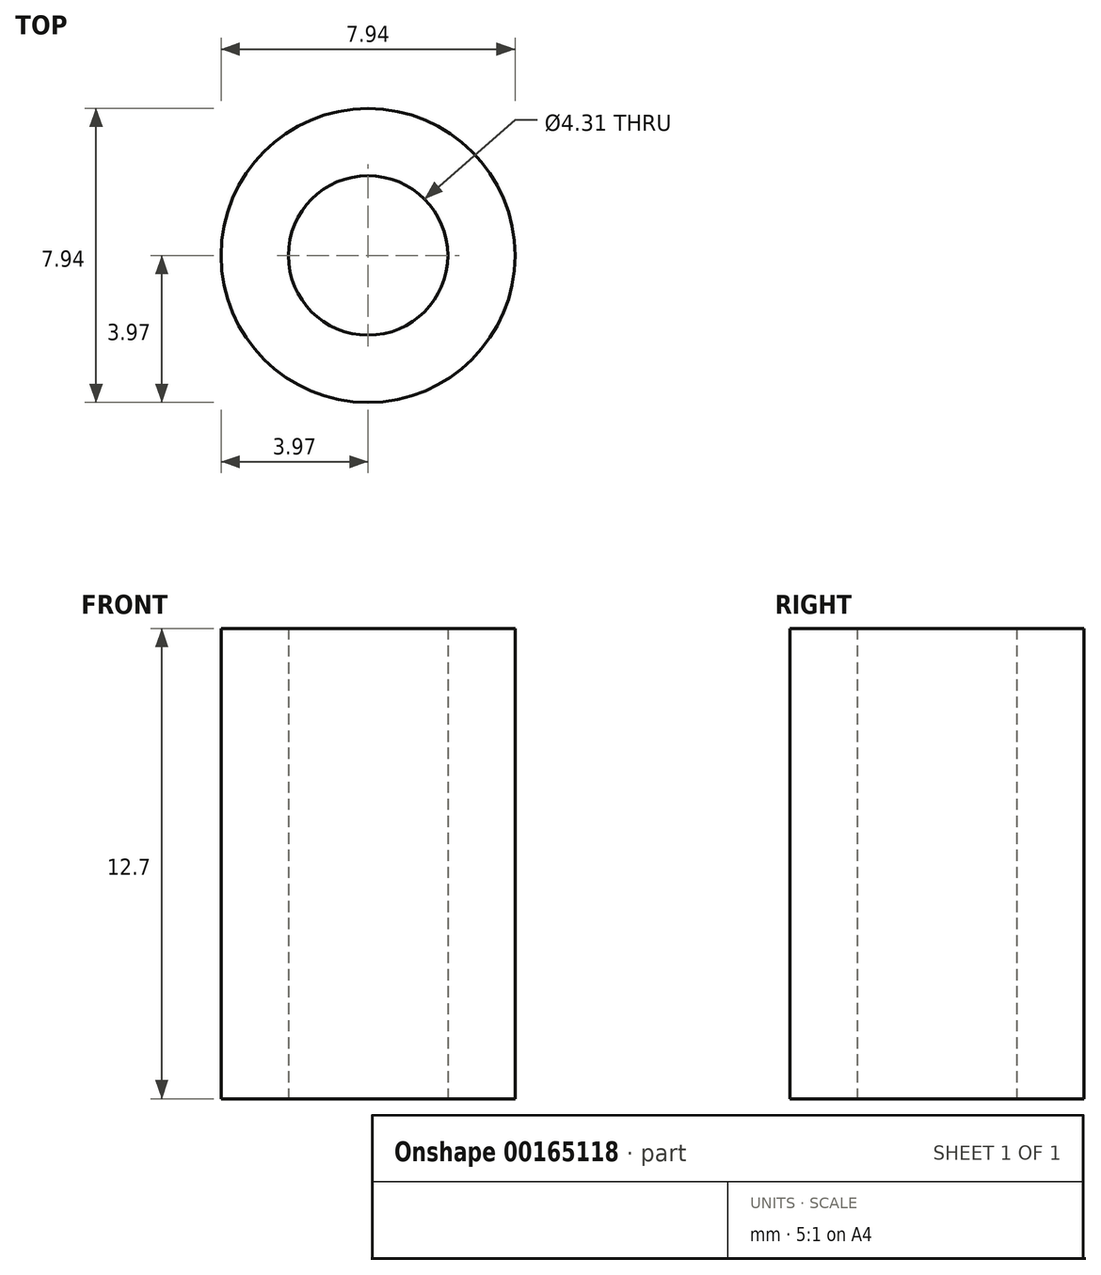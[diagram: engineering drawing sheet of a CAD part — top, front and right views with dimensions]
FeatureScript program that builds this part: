
annotation { "Feature Type Name" : "Feature", "Feature Type Description" : "" }
export const myFeature = defineFeature(function(context is Context, id is Id, definition is map)
    precondition{}
    {
        {
            var Q0;
            Q0=qCreatedBy(makeId("Top.planeOp"),FACE);
            var sketch = newSketch(context, id + "F0", { "sketchPlane" : qUnion([Q0])});
            skCircle(sketch, "E0", {"center": v(0, 0) * mm, "radius": 2.15 * mm});
            skCircle(sketch, "E1", {"center": v(0, 0) * mm, "radius": 3.97 * mm});
            skSolve(sketch);
        }
        {
            var Q0;
            Q0=qSketchRegion(id+"F0",true);
            extrude(context, id + "F1", {"entities" : qUnion([Q0]), "depth" : 12.7 * mm});
        }
    });
